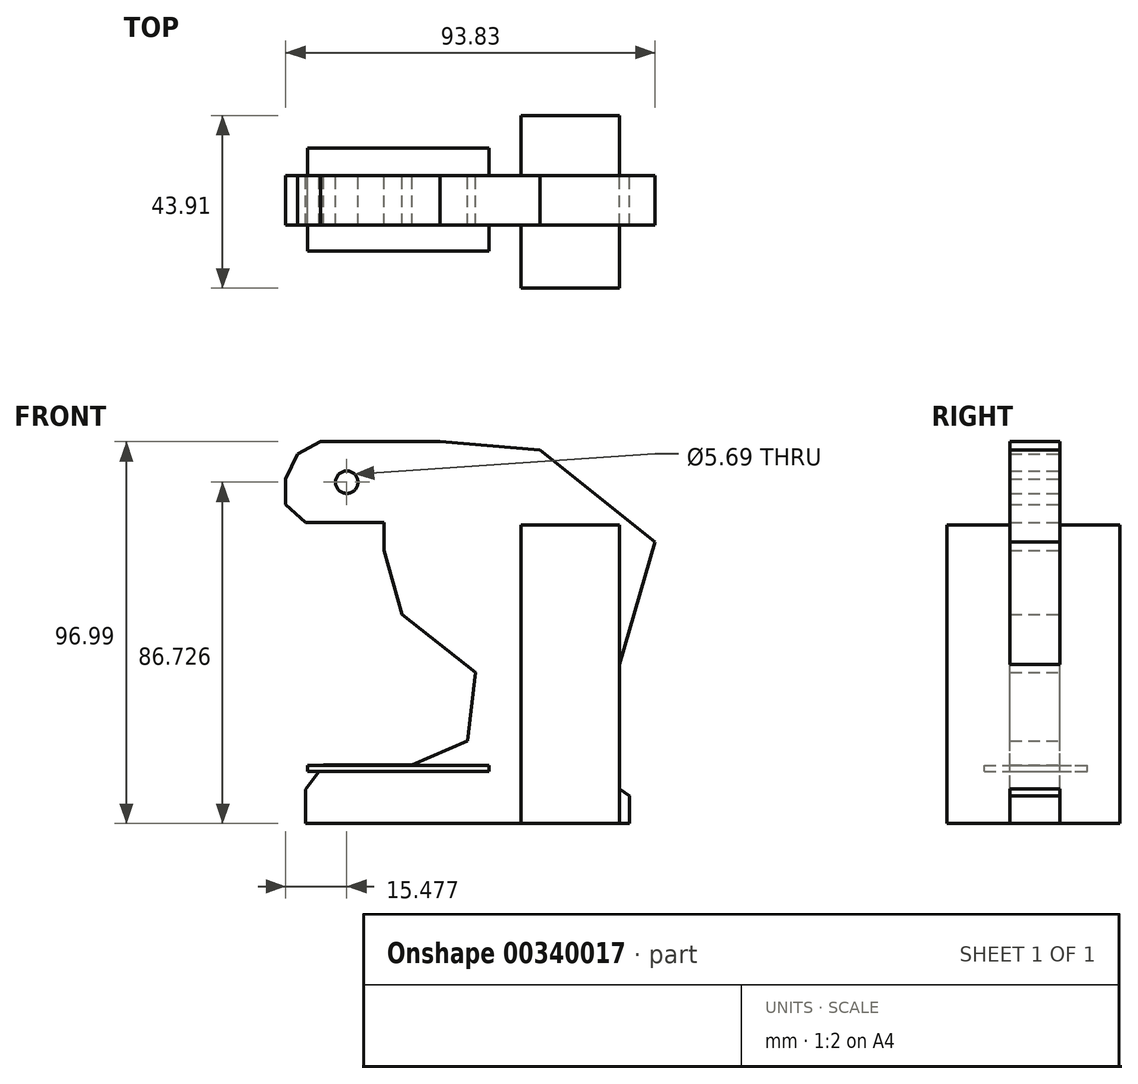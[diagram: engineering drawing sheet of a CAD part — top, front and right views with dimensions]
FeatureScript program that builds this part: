
annotation { "Feature Type Name" : "Feature", "Feature Type Description" : "" }
export const myFeature = defineFeature(function(context is Context, id is Id, definition is map)
    precondition{}
    {
        {
            var Q0;
            Q0=qCreatedBy(makeId("Front.planeOp"),FACE);
            var sketch = newSketch(context, id + "F0", { "sketchPlane" : qUnion([Q0])});
            skLineSegment(sketch, "E0", {"start": v(45.65, -55.05) * mm, "end": v(52.6, -59.95) * mm});
            skLineSegment(sketch, "E1", {"start": v(52.6, -59.95) * mm, "end": v(52.6, -66.9) * mm});
            skLineSegment(sketch, "E2", {"start": v(52.6, -66.9) * mm, "end": v(-29.7, -66.9) * mm});
            skLineSegment(sketch, "E3", {"start": v(-29.7, -66.9) * mm, "end": v(-29.7, -58.21) * mm});
            skLineSegment(sketch, "E4", {"start": v(-29.7, -58.21) * mm, "end": v(-25.12, -52.05) * mm});
            skLineSegment(sketch, "E5", {"start": v(-25.12, -52.05) * mm, "end": v(-2.69, -52.05) * mm});
            skLineSegment(sketch, "E6", {"start": v(-2.69, -52.05) * mm, "end": v(11.37, -45.9) * mm});
            skLineSegment(sketch, "E7", {"start": v(11.37, -45.9) * mm, "end": v(13.43, -28.51) * mm});
            skLineSegment(sketch, "E8", {"start": v(13.43, -28.51) * mm, "end": v(-5.21, -13.82) * mm});
            skLineSegment(sketch, "E9", {"start": v(-5.21, -13.82) * mm, "end": v(-9.8, 2.45) * mm});
            skLineSegment(sketch, "E10", {"start": v(-9.8, 2.45) * mm, "end": v(-9.8, 9.56) * mm});
            skLineSegment(sketch, "E11", {"start": v(-9.8, 9.56) * mm, "end": v(-29.7, 9.56) * mm});
            skLineSegment(sketch, "E12", {"start": v(-29.7, 9.56) * mm, "end": v(-34.75, 14.14) * mm});
            skLineSegment(sketch, "E13", {"start": v(-34.75, 14.14) * mm, "end": v(-34.75, 20.62) * mm});
            skLineSegment(sketch, "E14", {"start": v(-34.75, 20.62) * mm, "end": v(-31.75, 26.93) * mm});
            skLineSegment(sketch, "E15", {"start": v(-31.75, 26.93) * mm, "end": v(-25.9, 30.1) * mm});
            skLineSegment(sketch, "E16", {"start": v(-25.9, 30.1) * mm, "end": v(4.42, 30.1) * mm});
            skLineSegment(sketch, "E17", {"start": v(4.42, 30.1) * mm, "end": v(29.86, 28.04) * mm});
            skLineSegment(sketch, "E18", {"start": v(29.86, 28.04) * mm, "end": v(59.08, 4.66) * mm});
            skLineSegment(sketch, "E19", {"start": v(59.08, 4.66) * mm, "end": v(49.76, -27.25) * mm});
            skLineSegment(sketch, "E20", {"start": v(49.76, -27.25) * mm, "end": v(45.65, -55.05) * mm});
            skCircle(sketch, "E21", {"center": v(-19.27, 19.83) * mm, "radius": 2.84 * mm});
            skSolve(sketch);
        }
        {
            var Q0;
            Q0 = qSketchRegion(id + "F0", true);
            extrude(context, id + "F1", {"entities" : qUnion([Q0]), "depth" : 12.6 * mm});
        }
        {
            var Q0;
            Q0=qCreatedBy(makeId("Right.planeOp"),FACE);
            cPlane(context, id + "F2", {"entities" : qUnion([Q0]), "cplaneType" : CPlaneType.OFFSET, "offset" : 25 * mm, "width" : 150 * mm, "height" : 150 * mm});
        }
        {
            var Q0;
            Q0=qCreatedBy(id+"F2.planeOp",FACE);
            var sketch = newSketch(context, id + "F3", { "sketchPlane" : qUnion([Q0])});
            skLineSegment(sketch, "E22.bottom", {"start": v(-28.6, 8.93) * mm, "end": v(15.32, 8.93) * mm});
            skLineSegment(sketch, "E22.top", {"start": v(-28.6, -66.9) * mm, "end": v(15.32, -66.9) * mm});
            skLineSegment(sketch, "E22.left", {"start": v(-28.6, 8.93) * mm, "end": v(-28.6, -66.9) * mm});
            skLineSegment(sketch, "E22.right", {"start": v(15.32, 8.93) * mm, "end": v(15.32, -66.9) * mm});
            skSolve(sketch);
        }
        {
            var Q0;
            Q0 = qSketchRegion(id + "F3", true);
            extrude(context, id + "F4", {"entities" : qUnion([Q0]), "operationType" : NewBodyOperationType.ADD, "depth" : 25 * mm});
        }
        {
            var Q0;
            Q0=qCreatedBy(makeId("Top.planeOp"),FACE);
            cPlane(context, id + "F5", {"entities" : qUnion([Q0]), "cplaneType" : CPlaneType.OFFSET, "offset" : 52.2 * mm, "oppositeDirection" : true, "width" : 150 * mm, "height" : 150 * mm});
        }
        {
            var Q0;
            Q0=qCreatedBy(id+"F5.planeOp",FACE);
            var sketch = newSketch(context, id + "F6", { "sketchPlane" : qUnion([Q0])});
            skLineSegment(sketch, "E23.bottom", {"start": v(-29.23, -19.2) * mm, "end": v(16.9, -19.2) * mm});
            skLineSegment(sketch, "E23.top", {"start": v(-29.23, 7.03) * mm, "end": v(16.9, 7.03) * mm});
            skLineSegment(sketch, "E23.left", {"start": v(-29.23, -19.2) * mm, "end": v(-29.23, 7.03) * mm});
            skLineSegment(sketch, "E23.right", {"start": v(16.9, -19.2) * mm, "end": v(16.9, 7.03) * mm});
            skSolve(sketch);
        }
        {
            var Q0;
            Q0 = qSketchRegion(id + "F6", true);
            extrude(context, id + "F7", {"entities" : qUnion([Q0]), "operationType" : NewBodyOperationType.ADD, "oppositeDirection" : true, "depth" : 1.5 * mm});
        }
    });
